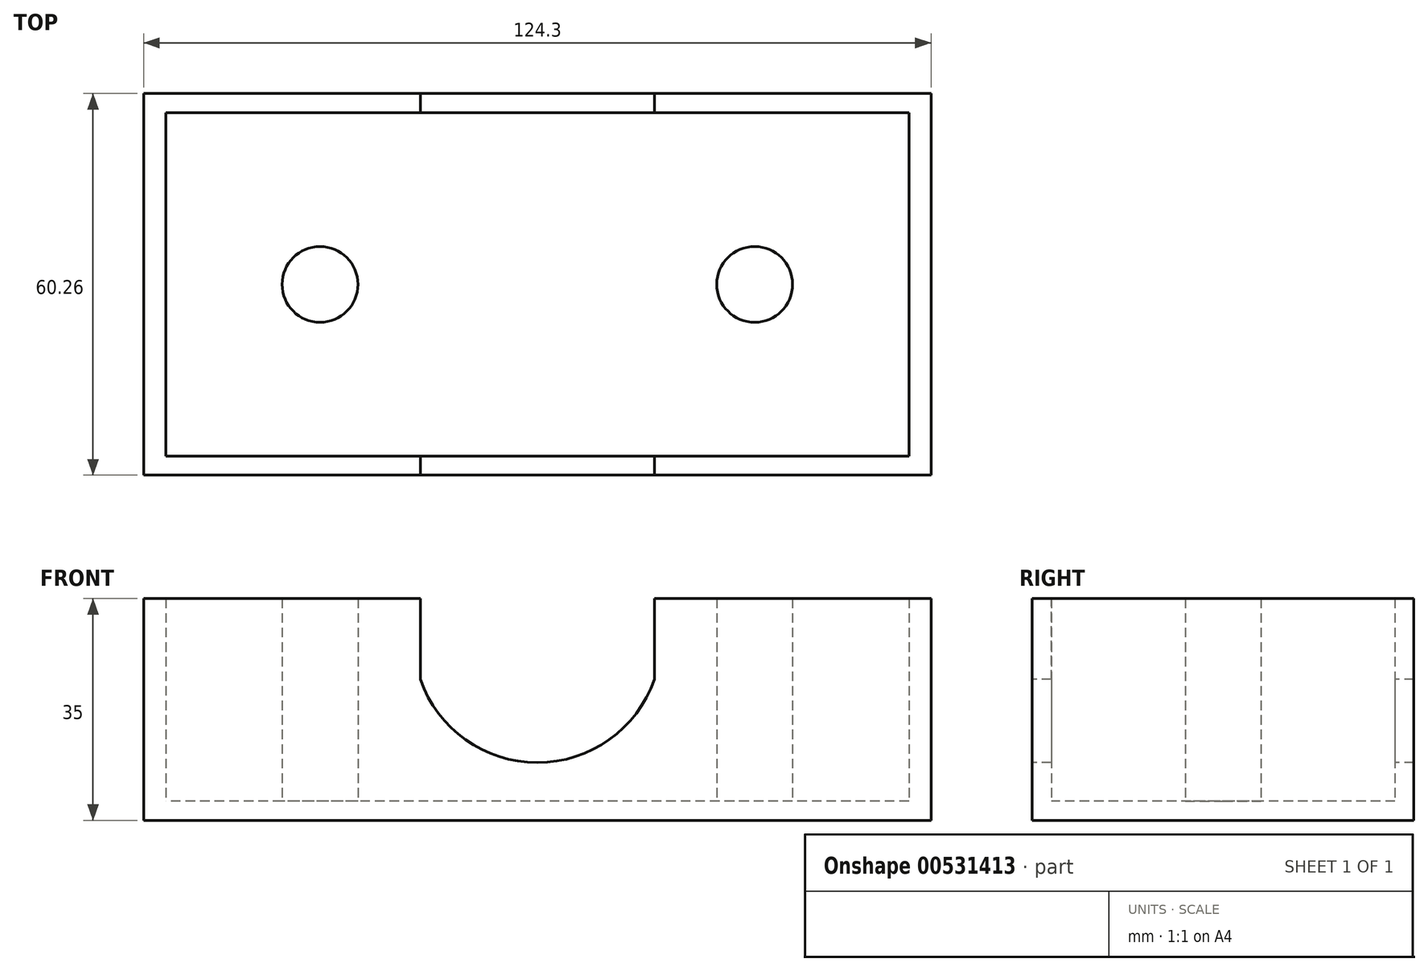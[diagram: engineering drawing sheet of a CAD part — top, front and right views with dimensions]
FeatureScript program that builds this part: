
annotation { "Feature Type Name" : "Feature", "Feature Type Description" : "" }
export const myFeature = defineFeature(function(context is Context, id is Id, definition is map)
    precondition{}
    {
        {
            var Q0;
            Q0=qCreatedBy(makeId("Top.planeOp"),FACE);
            var sketch = newSketch(context, id + "F0", { "sketchPlane" : qUnion([Q0])});
            skLineSegment(sketch, "E0.bottom", {"start": v(58.66, 27.13) * mm, "end": v(-58.66, 27.13) * mm});
            skLineSegment(sketch, "E0.top", {"start": v(58.66, -27.13) * mm, "end": v(-58.66, -27.13) * mm});
            skLineSegment(sketch, "E0.left", {"start": v(58.66, 27.13) * mm, "end": v(58.66, -27.13) * mm});
            skLineSegment(sketch, "E0.right", {"start": v(-58.66, 27.13) * mm, "end": v(-58.66, -27.13) * mm});
            skPoint(sketch, "E0.middle", {"position": v(0, 0) * mm});
            skSolve(sketch);
        }
        {
            var Q0;
            Q0 = qSketchRegion(id + "F0", true);
            extrude(context, id + "F1", {"entities" : qUnion([Q0]), "depth" : 3 * mm, "offsetDistance" : 25 * mm});
        }
        {
            var Q0;
            Q0=qCreatedBy(makeId("Top.planeOp"),FACE);
            var sketch = newSketch(context, id + "F2", { "sketchPlane" : qUnion([Q0])});
            skLineSegment(sketch, "E1.0.0", {"start": v(-58.66, -27.13) * mm, "end": v(58.66, -27.13) * mm});
            skLineSegment(sketch, "E1.0.1", {"start": v(58.66, -27.13) * mm, "end": v(58.66, 27.13) * mm});
            skLineSegment(sketch, "E1.0.2", {"start": v(58.66, 27.13) * mm, "end": v(-58.66, 27.13) * mm});
            skLineSegment(sketch, "E1.0.3", {"start": v(-58.66, 27.13) * mm, "end": v(-58.66, -27.13) * mm});
            skLineSegment(sketch, "E2.bottom", {"start": v(62.15, 30.13) * mm, "end": v(-62.15, 30.13) * mm});
            skLineSegment(sketch, "E2.top", {"start": v(62.15, -30.13) * mm, "end": v(-62.15, -30.13) * mm});
            skLineSegment(sketch, "E2.left", {"start": v(62.15, 30.13) * mm, "end": v(62.15, -30.13) * mm});
            skLineSegment(sketch, "E2.right", {"start": v(-62.15, 30.13) * mm, "end": v(-62.15, -30.13) * mm});
            skPoint(sketch, "E2.middle", {"position": v(0, 0) * mm});
            skCircle(sketch, "E3", {"center": v(-41.73, 0) * mm, "radius": 6.7 * mm});
            skCircle(sketch, "E4.MirrorC", {"center": v(41.73, 0) * mm, "radius": 6.7 * mm});
            skSolve(sketch);
        }
        {
            var Q0;
            Q0 = qSketchRegion(id + "F2", true);
            extrude(context, id + "F3", {"entities" : qUnion([Q0]), "operationType" : NewBodyOperationType.ADD, "depth" : 35 * mm, "offsetDistance" : 25 * mm});
        }
        {
            var Q0;
            Q0=qCreatedBy(makeId("Top.planeOp"),FACE);
            var sketch = newSketch(context, id + "F4", { "sketchPlane" : qUnion([Q0])});
            skCircle(sketch, "E5", {"center": v(-34.32, 0) * mm, "radius": 5.98 * mm});
            skCircle(sketch, "E6.MirrorC", {"center": v(34.32, 0) * mm, "radius": 5.98 * mm});
            skSolve(sketch);
        }
        {
            var Q0;
            Q0 = qSketchRegion(id + "F4", true);
            extrude(context, id + "F5", {"entities" : qUnion([Q0]), "operationType" : NewBodyOperationType.ADD, "depth" : 35 * mm, "offsetDistance" : 25 * mm});
        }
        {
            var Q0;
            Q0=qCreatedBy(makeId("Front.planeOp"),FACE);
            var sketch = newSketch(context, id + "F6", { "sketchPlane" : qUnion([Q0])});
            skLineSegment(sketch, "E7.0.0", {"start": v(-62.15, 0) * mm, "end": v(62.15, 0) * mm, "construction": true});
            skLineSegment(sketch, "E7.0.1", {"start": v(62.15, 0) * mm, "end": v(62.15, 35) * mm, "construction": true});
            skLineSegment(sketch, "E7.0.2", {"start": v(62.15, 35) * mm, "end": v(-62.15, 35) * mm, "construction": true});
            skLineSegment(sketch, "E7.0.3", {"start": v(-62.15, 35) * mm, "end": v(-62.15, 0) * mm, "construction": true});
            skLineSegment(sketch, "E8", {"start": v(-18.5, 35) * mm, "end": v(-18.5, 22.24) * mm});
            skLineSegment(sketch, "E9.MirrorCS", {"start": v(18.5, 35) * mm, "end": v(18.5, 22.24) * mm});
            skArc(sketch, "E10", {"start": v(-18.5, 22.24) * mm, "mid": v(0, 9.12) * mm, "end": v(18.5, 22.24) * mm});
            skLineSegment(sketch, "E11", {"start": v(-18.5, 35) * mm, "end": v(18.5, 35) * mm});
            skSolve(sketch);
        }
        {
            var Q0;
            Q0 = qSketchRegion(id + "F6", true);
            extrude(context, id + "F7", {"entities" : qUnion([Q0]), "operationType" : NewBodyOperationType.REMOVE, "endBound" : BoundingType.THROUGH_ALL, "oppositeDirection" : true, "depth" : 25 * mm, "offsetDistance" : 25 * mm, "hasSecondDirection" : true, "secondDirectionBound" : SecondDirectionBoundingType.THROUGH_ALL, "secondDirectionOppositeDirection" : false, "secondDirectionDepth" : 25 * mm});
        }
    });
